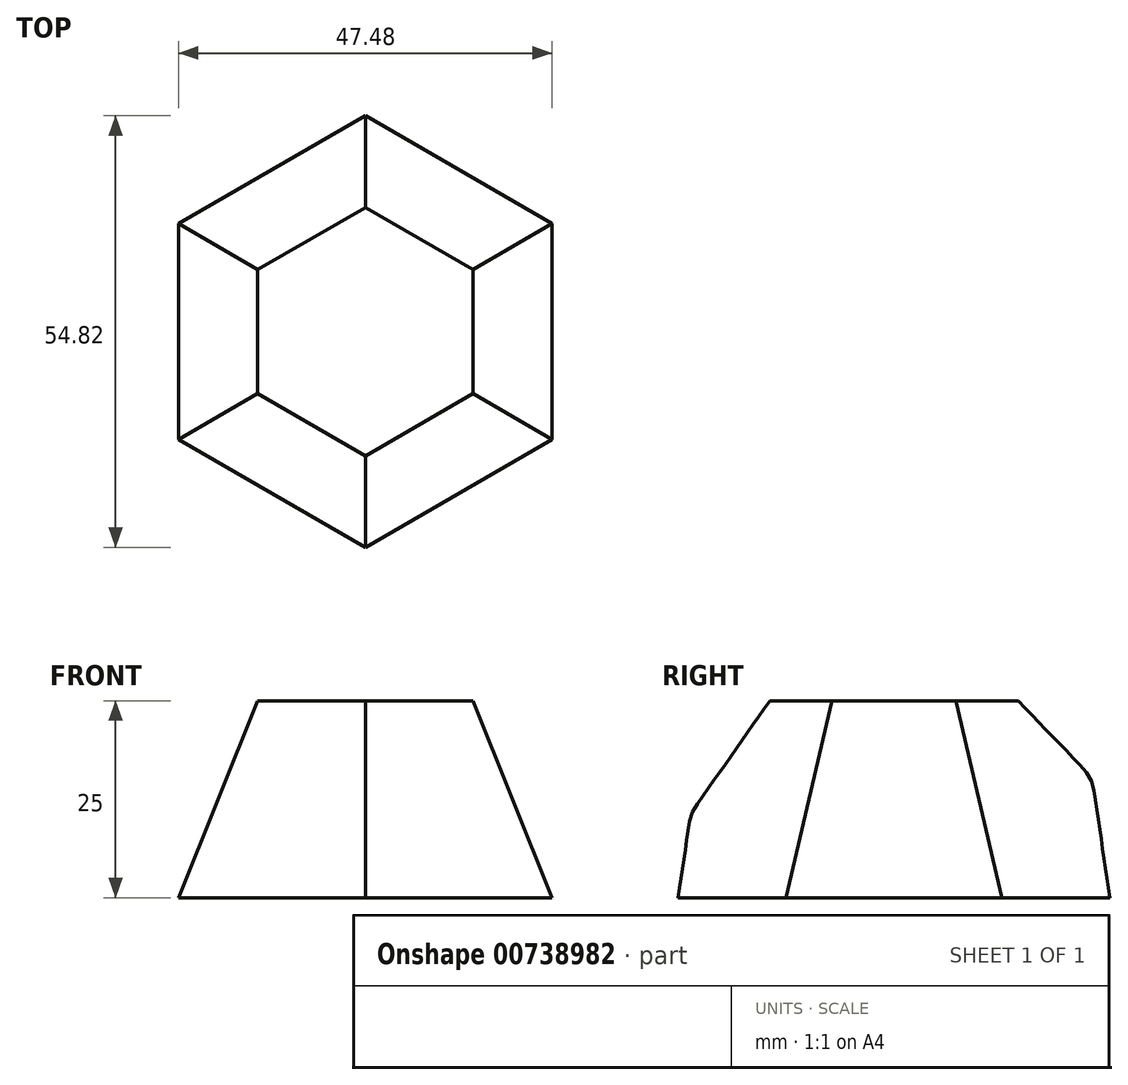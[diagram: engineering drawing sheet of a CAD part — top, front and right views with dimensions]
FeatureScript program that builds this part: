
annotation { "Feature Type Name" : "Feature", "Feature Type Description" : "" }
export const myFeature = defineFeature(function(context is Context, id is Id, definition is map)
    precondition{}
    {
        {
            var Q0;
            Q0=qCreatedBy(makeId("Top.planeOp"),FACE);
            var sketch = newSketch(context, id + "F0", { "sketchPlane" : qUnion([Q0])});
            skCircle(sketch, "E0.cCircle", {"center": v(0, 0) * mm, "radius": 23.74 * mm, "construction": true});
            skLineSegment(sketch, "E0.0", {"start": v(-23.74, 13.7) * mm, "end": v(0, 27.41) * mm});
            skLineSegment(sketch, "E0.1", {"start": v(0, 27.41) * mm, "end": v(23.74, 13.7) * mm});
            skLineSegment(sketch, "E0.2", {"start": v(23.74, 13.7) * mm, "end": v(23.74, -13.7) * mm});
            skLineSegment(sketch, "E0.3", {"start": v(23.74, -13.7) * mm, "end": v(0, -27.41) * mm});
            skLineSegment(sketch, "E0.4", {"start": v(0, -27.41) * mm, "end": v(-23.74, -13.7) * mm});
            skLineSegment(sketch, "E0.5", {"start": v(-23.74, -13.7) * mm, "end": v(-23.74, 13.7) * mm});
            skPoint(sketch, "E0.0.midPoint", {"position": v(-11.87, 20.56) * mm});
            skSolve(sketch);
        }
        {
            var Q0;
            Q0=qCreatedBy(makeId("Top.planeOp"),FACE);
            cPlane(context, id + "F1", {"entities" : qUnion([Q0]), "cplaneType" : CPlaneType.OFFSET, "offset" : 25 * mm, "width" : 150 * mm, "height" : 150 * mm});
        }
        {
            var Q0;
            Q0=qCreatedBy(id+"F1.planeOp",FACE);
            var sketch = newSketch(context, id + "F2", { "sketchPlane" : qUnion([Q0])});
            skCircle(sketch, "E1.cCircle", {"center": v(0, 0) * mm, "radius": 13.67 * mm, "construction": true});
            skLineSegment(sketch, "E1.0", {"start": v(-13.67, 7.9) * mm, "end": v(0, 15.78) * mm});
            skLineSegment(sketch, "E1.1", {"start": v(0, 15.78) * mm, "end": v(13.67, 7.9) * mm});
            skLineSegment(sketch, "E1.2", {"start": v(13.67, 7.9) * mm, "end": v(13.67, -7.9) * mm});
            skLineSegment(sketch, "E1.3", {"start": v(13.67, -7.9) * mm, "end": v(0, -15.78) * mm});
            skLineSegment(sketch, "E1.4", {"start": v(0, -15.78) * mm, "end": v(-13.67, -7.9) * mm});
            skLineSegment(sketch, "E1.5", {"start": v(-13.67, -7.9) * mm, "end": v(-13.67, 7.9) * mm});
            skPoint(sketch, "E1.0.midPoint", {"position": v(-6.83, 11.84) * mm});
            skSolve(sketch);
        }
        {
            var Q0;
            Q0=qCreatedBy(makeId("Right.planeOp"),FACE);
            var sketch = newSketch(context, id + "F3", { "sketchPlane" : qUnion([Q0])});
            skLineSegment(sketch, "E2", {"start": v(27.41, 0) * mm, "end": v(25.41, 13.65) * mm});
            skLineSegment(sketch, "E3", {"start": v(24.07, 16.4) * mm, "end": v(15.78, 25) * mm});
            skPoint(sketch, "E4.visualSharp", {"position": v(25.18, 15.24) * mm});
            skArc(sketch, "E4.filletArc", {"start": v(25.41, 13.65) * mm, "mid": v(24.95, 15.13) * mm, "end": v(24.07, 16.4) * mm});
            skSolve(sketch);
        }
        {
            var Q0;
            Q0=qCreatedBy(makeId("Right.planeOp"),FACE);
            var sketch = newSketch(context, id + "F4", { "sketchPlane" : qUnion([Q0])});
            skLineSegment(sketch, "E5", {"start": v(-15.78, 25) * mm, "end": v(-25.14, 11.66) * mm});
            skLineSegment(sketch, "E6", {"start": v(-26, 9.53) * mm, "end": v(-27.41, 0) * mm});
            skPoint(sketch, "E7.visualSharp", {"position": v(-25.82, 10.7) * mm});
            skArc(sketch, "E7.filletArc", {"start": v(-25.14, 11.66) * mm, "mid": v(-25.7, 10.64) * mm, "end": v(-26, 9.53) * mm});
            skSolve(sketch);
        }
        {
            var Q0;
            Q0 = qSketchRegion(id + "F0", true);
            var Q1;
            Q1 = qSketchRegion(id + "F2", true);
            var Q2;
            Q2 = qConstructionFilter(qBodyType(qCreatedBy(id + "F3" ,EDGE), BodyType.WIRE), ConstructionObject.NO);
            var Q3;
            Q3 = qConstructionFilter(qBodyType(qCreatedBy(id + "F4" ,EDGE), BodyType.WIRE), ConstructionObject.NO);
            loft(context, id + "F5", {"addGuides" : true, "sheetProfilesArray" : [{ "sheetProfileEntities" : qUnion([Q0]) }, { "sheetProfileEntities" : qUnion([Q1]) }], "guidesArray" : [{ "guideEntities" : qUnion([Q2]), "guideDerivativeType" : LoftGuideDerivativeType.DEFAULT, "guideDerivativeMagnitude" : 1 }, { "guideEntities" : qUnion([Q3]), "guideDerivativeType" : LoftGuideDerivativeType.DEFAULT, "guideDerivativeMagnitude" : 1 }]});
        }
    });
